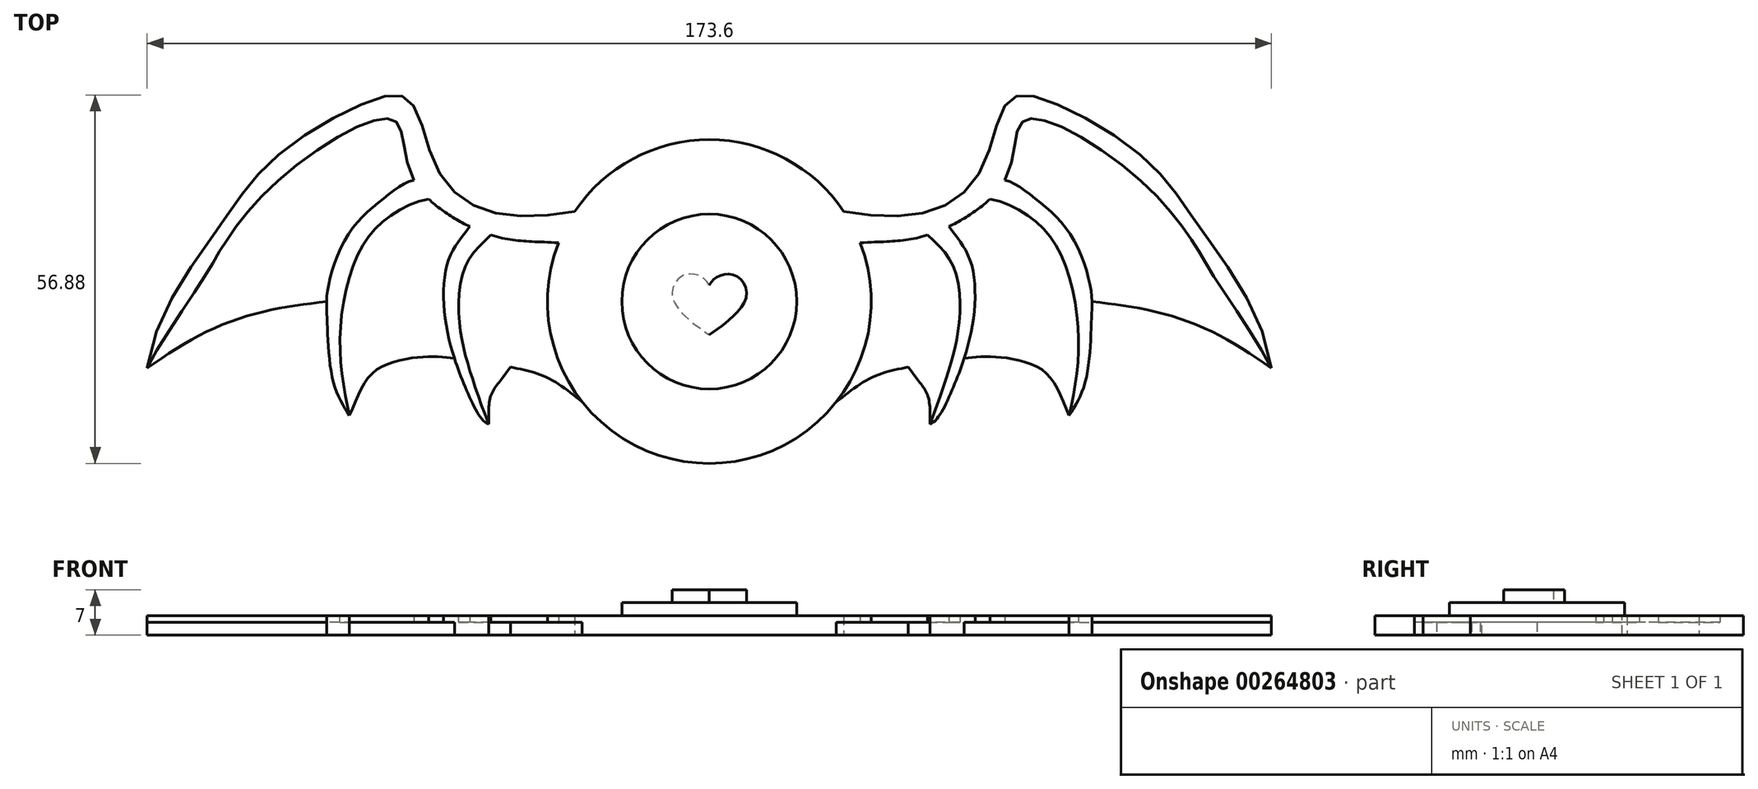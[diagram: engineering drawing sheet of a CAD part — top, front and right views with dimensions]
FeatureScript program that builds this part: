
annotation { "Feature Type Name" : "Feature", "Feature Type Description" : "" }
export const myFeature = defineFeature(function(context is Context, id is Id, definition is map)
    precondition{}
    {
        {
            var Q0;
            Q0=qCreatedBy(makeId("Top.planeOp"),FACE);
            var sketch = newSketch(context, id + "F0", { "sketchPlane" : qUnion([Q0])});
            skCircle(sketch, "E0", {"center": v(0, 0) * mm, "radius": 25 * mm});
            skLineSegment(sketch, "E1", {"start": v(0, 25) * mm, "end": v(0, -25) * mm, "construction": true});
            skFitSpline(sketch, "E2", {"points": [v(20.76, 13.92) * mm, v(34.08, 13.92) * mm, v(42, 20.48) * mm, v(46, 30.69) * mm, v(50.93, 31.48) * mm, v(67.03, 22.24) * mm, v(75.74, 11.46) * mm, v(86.8, -10.28) * mm], "startDerivative": vector(95.75, -17.53) * mm, "endDerivative": vector(18.54, -135.11) * mm});
            skFitSpline(sketch, "E3", {"points": [v(20.7, -14) * mm, v(37, -10.54) * mm, v(45, -8.07) * mm, v(66.66, 1.74) * mm, v(75.74, 11.46) * mm], "startDerivative": vector(59.46, -0.59) * mm, "endDerivative": vector(18.77, 28.66) * mm, "construction": true});
            skFitSpline(sketch, "E4", {"points": [v(23.3, 9.08) * mm, v(33.72, 10.28) * mm, v(45.64, 18.76) * mm, v(47.9, 27.18) * mm, v(51.1, 28.14) * mm, v(65.44, 19.69) * mm, v(74.45, 9.58) * mm, v(78.2, 3.43) * mm, v(86.8, -10.28) * mm], "startDerivative": vector(110.38, 5.87) * mm, "endDerivative": vector(40.39, -81.17) * mm});
            skFitSpline(sketch, "E5", {"points": [v(33.72, 10.28) * mm, v(37.86, 5.02) * mm, v(38.5, -3.9) * mm, v(37, -10.54) * mm, v(34.08, -18.9) * mm], "startDerivative": vector(21.3, -19.5) * mm, "endDerivative": vector(-13.55, -34.2) * mm});
            skFitSpline(sketch, "E6", {"points": [v(37, 11.6) * mm, v(40.25, 6.46) * mm, v(40.52, -4.24) * mm, v(37.2, -14.33) * mm, v(34.08, -18.9) * mm], "startDerivative": vector(14.85, -22) * mm, "endDerivative": vector(-16.96, -5.17) * mm});
            skFitSpline(sketch, "E7", {"points": [v(32.11, -12.01) * mm, v(33.72, -14.49) * mm, v(34.08, -18.9) * mm], "startDerivative": vector(4.43, -5.79) * mm, "endDerivative": vector(-0.15, -8.8) * mm});
            skFitSpline(sketch, "E8", {"points": [v(45.64, 18.76) * mm, v(50.26, 15.97) * mm, v(55.72, 10.44) * mm, v(58.9, 2) * mm, v(59.02, -2.64) * mm, v(58.1, -12.2) * mm, v(55.56, -17.62) * mm], "startDerivative": vector(28.21, -5.42) * mm, "endDerivative": vector(-19.1, -30.2) * mm});
            skFitSpline(sketch, "E9", {"points": [v(43.34, 15.84) * mm, v(49.55, 13.02) * mm, v(53.96, 7.9) * mm, v(56.67, -1.36) * mm, v(56.83, -10.28) * mm, v(55.56, -17.62) * mm], "startDerivative": vector(32.47, -4.35) * mm, "endDerivative": vector(-7.91, -36.84) * mm});
            skFitSpline(sketch, "E10", {"points": [v(38.97, -9.94) * mm, v(46.63, -10.28) * mm, v(52.84, -13.22) * mm, v(55.56, -17.62) * mm], "startDerivative": vector(21.38, 0.7) * mm, "endDerivative": vector(7.12, -15.9) * mm, "construction": true});
            skFitSpline(sketch, "E11", {"points": [v(59.1, 0) * mm, v(68, -1.36) * mm, v(77.72, -4.7) * mm, v(86.8, -10.28) * mm], "startDerivative": vector(27.78, -3.23) * mm, "endDerivative": vector(25.67, -17.5) * mm});
            skFitSpline(sketch, "E12", {"points": [v(19.62, -15.5) * mm, v(25.1, -11.72) * mm, v(30.69, -10.12) * mm], "startDerivative": vector(10.4, 8.3) * mm, "endDerivative": vector(11.78, 2.35) * mm});
            skFitSpline(sketch, "E13", {"points": [v(32.11, -12.01) * mm, v(30.69, -10.12) * mm], "startDerivative": vector(-1.42, 1.9) * mm, "endDerivative": vector(-1.42, 1.9) * mm});
            skFitSpline(sketch, "E14", {"points": [v(55.56, -17.62) * mm, v(52.05, -11.08) * mm, v(46.6, -8.83) * mm, v(42.13, -8.5) * mm, v(39.36, -8.79) * mm], "startDerivative": vector(-10.96, 25.87) * mm, "endDerivative": vector(-14.04, -2.02) * mm});
            skFitSpline(sketch, "E15", {"points": [v(20.76, 13.92) * mm, v(16.18, 9.49) * mm, v(19.62, -15.5) * mm], "startDerivative": vector(-16.85, -9.2) * mm, "endDerivative": vector(11.44, -45.62) * mm});
            skFitSpline(sketch, "E16.MirrorCS", {"points": [v(-20.76, 13.92) * mm, v(-16.18, 9.49) * mm, v(-19.62, -15.5) * mm], "startDerivative": vector(16.85, -9.2) * mm, "endDerivative": vector(-11.44, -45.62) * mm});
            skFitSpline(sketch, "E17.MirrorCS", {"points": [v(-23.3, 9.08) * mm, v(-33.72, 10.28) * mm, v(-45.64, 18.76) * mm, v(-47.9, 27.18) * mm, v(-51.1, 28.14) * mm, v(-65.44, 19.69) * mm, v(-74.45, 9.58) * mm, v(-78.2, 3.43) * mm, v(-86.8, -10.28) * mm], "startDerivative": vector(-110.38, 5.87) * mm, "endDerivative": vector(-40.39, -81.17) * mm});
            skFitSpline(sketch, "E18.MirrorCS", {"points": [v(-20.76, 13.92) * mm, v(-34.08, 13.92) * mm, v(-42, 20.48) * mm, v(-46, 30.69) * mm, v(-50.93, 31.48) * mm, v(-67.03, 22.24) * mm, v(-75.74, 11.46) * mm, v(-86.8, -10.28) * mm], "startDerivative": vector(-95.75, -17.53) * mm, "endDerivative": vector(-18.54, -135.11) * mm});
            skFitSpline(sketch, "E19.MirrorCS", {"points": [v(-33.72, 10.28) * mm, v(-37.86, 5.02) * mm, v(-38.5, -3.9) * mm, v(-37, -10.54) * mm, v(-34.08, -18.9) * mm], "startDerivative": vector(-21.3, -19.5) * mm, "endDerivative": vector(13.55, -34.2) * mm});
            skFitSpline(sketch, "E20.MirrorCS", {"points": [v(-37, 11.6) * mm, v(-40.25, 6.46) * mm, v(-40.52, -4.24) * mm, v(-37.2, -14.33) * mm, v(-34.08, -18.9) * mm], "startDerivative": vector(-14.85, -22) * mm, "endDerivative": vector(16.96, -5.17) * mm});
            skFitSpline(sketch, "E21.MirrorCS", {"points": [v(-43.34, 15.84) * mm, v(-49.55, 13.02) * mm, v(-53.96, 7.9) * mm, v(-56.67, -1.36) * mm, v(-56.83, -10.28) * mm, v(-55.56, -17.62) * mm], "startDerivative": vector(-32.47, -4.35) * mm, "endDerivative": vector(7.91, -36.84) * mm});
            skFitSpline(sketch, "E22.MirrorCS", {"points": [v(-45.64, 18.76) * mm, v(-50.26, 15.97) * mm, v(-55.72, 10.44) * mm, v(-58.9, 2) * mm, v(-59.02, -2.64) * mm, v(-58.1, -12.2) * mm, v(-55.56, -17.62) * mm], "startDerivative": vector(-28.21, -5.42) * mm, "endDerivative": vector(19.1, -30.2) * mm});
            skFitSpline(sketch, "E23.MirrorCS", {"points": [v(-19.62, -15.5) * mm, v(-25.1, -11.72) * mm, v(-30.69, -10.12) * mm], "startDerivative": vector(-10.4, 8.3) * mm, "endDerivative": vector(-11.78, 2.35) * mm});
            skFitSpline(sketch, "E24.MirrorCS", {"points": [v(-32.11, -12.01) * mm, v(-30.69, -10.12) * mm], "startDerivative": vector(1.42, 1.9) * mm, "endDerivative": vector(1.42, 1.9) * mm});
            skFitSpline(sketch, "E25.MirrorCS", {"points": [v(-32.11, -12.01) * mm, v(-33.72, -14.49) * mm, v(-34.08, -18.9) * mm], "startDerivative": vector(-4.43, -5.79) * mm, "endDerivative": vector(0.15, -8.8) * mm});
            skFitSpline(sketch, "E26.MirrorCS", {"points": [v(-59.1, 0) * mm, v(-68, -1.36) * mm, v(-77.72, -4.7) * mm, v(-86.8, -10.28) * mm], "startDerivative": vector(-27.78, -3.23) * mm, "endDerivative": vector(-25.67, -17.5) * mm});
            skFitSpline(sketch, "E27.MirrorCS", {"points": [v(-55.56, -17.62) * mm, v(-52.05, -11.08) * mm, v(-46.6, -8.83) * mm, v(-42.13, -8.5) * mm, v(-39.36, -8.79) * mm], "startDerivative": vector(10.96, 25.87) * mm, "endDerivative": vector(14.04, -2.02) * mm});
            skSolve(sketch);
        }
        {
            var Q0;
            {var subQ0=sQuery(id+"F0.wireOp",EDGE,"E15");Q0=makeQuery(id+"F0.imprint","IMPRINT",FACE,{"disambiguationData":[TD([[makeQuery(id+"F0.imprint","IMPRINT",EDGE,{"derivedFrom":subQ0}),-1.0]])]});}
            var Q1;
            {var subQ0=sQuery(id+"F0.wireOp",EDGE,"E15");Q1=makeQuery(id+"F0.imprint","IMPRINT",FACE,{"disambiguationData":[TD([[makeQuery(id+"F0.imprint","IMPRINT",EDGE,{"derivedFrom":subQ0}),1.0]])]});}
            var Q2;
            {var subQ0=sQuery(id+"F0.wireOp",EDGE,"E16.MirrorCS");Q2=makeQuery(id+"F0.imprint","IMPRINT",FACE,{"disambiguationData":[TD([[makeQuery(id+"F0.imprint","IMPRINT",EDGE,{"derivedFrom":subQ0}),-1.0]])]});}
            extrude(context, id + "F1", {"entities" : qUnion([Q0, Q1, Q2]), "depth" : 3 * mm, "offsetDistance" : 25 * mm});
        }
        {
            var Q0;
            Q0=qCreatedBy(makeId("Top.planeOp"),FACE);
            var sketch = newSketch(context, id + "F2", { "sketchPlane" : qUnion([Q0])});
            skCircle(sketch, "E28", {"center": v(0, 0) * mm, "radius": 13.5 * mm});
            skSolve(sketch);
        }
        {
            var Q0;
            Q0=qSketchRegion(id+"F2",true);
            extrude(context, id + "F3", {"entities" : qUnion([Q0]), "operationType" : NewBodyOperationType.ADD, "depth" : 5 * mm, "offsetDistance" : 25 * mm});
        }
        {
            var Q0;
            {var subQ4=sQuery(id+"F0.wireOp",EDGE,"E2");Q0=makeQuery(id+"F0.imprint","IMPRINT",FACE,{"disambiguationData":[TD([[makeQuery(id+"F0.imprint","IMPRINT",EDGE,{"derivedFrom":subQ4}),-1.0]])]});}
            var Q1;
            {var subQ0=sQuery(id+"F0.wireOp",EDGE,"E15");Q1=makeQuery(id+"F0.imprint","IMPRINT",FACE,{"disambiguationData":[TD([[makeQuery(id+"F0.imprint","IMPRINT",EDGE,{"derivedFrom":subQ0}),1.0]])]});}
            var Q2;
            {var subQ0=sQuery(id+"F0.wireOp",EDGE,"E5");Q2=makeQuery(id+"F0.imprint","IMPRINT",FACE,{"disambiguationData":[TD([[makeQuery(id+"F0.imprint","IMPRINT",EDGE,{"derivedFrom":subQ0}),-1.0]])]});}
            var Q3;
            {var subQ0=sQuery(id+"F0.wireOp",EDGE,"E5");Q3=makeQuery(id+"F0.imprint","IMPRINT",FACE,{"disambiguationData":[TD([[makeQuery(id+"F0.imprint","IMPRINT",EDGE,{"derivedFrom":subQ0}),1.0]])]});}
            var Q4;
            {var subQ3=sQuery(id+"F0.wireOp",EDGE,"E9");Q4=makeQuery(id+"F0.imprint","IMPRINT",FACE,{"disambiguationData":[TD([[makeQuery(id+"F0.imprint","IMPRINT",EDGE,{"derivedFrom":subQ3}),-1.0]])]});}
            var Q5;
            {var subQ3=sQuery(id+"F0.wireOp",EDGE,"E9");Q5=makeQuery(id+"F0.imprint","IMPRINT",FACE,{"disambiguationData":[TD([[makeQuery(id+"F0.imprint","IMPRINT",EDGE,{"derivedFrom":subQ3}),1.0]])]});}
            var Q6;
            {var subQ0=sQuery(id+"F0.wireOp",EDGE,"E11");Q6=makeQuery(id+"F0.imprint","IMPRINT",FACE,{"disambiguationData":[TD([[makeQuery(id+"F0.imprint","IMPRINT",EDGE,{"derivedFrom":subQ0}),1.0]])]});}
            var Q7;
            {var subQ1=sQuery(id+"F0.wireOp",EDGE,"E19.MirrorCS");Q7=makeQuery(id+"F0.imprint","IMPRINT",FACE,{"disambiguationData":[TD([[makeQuery(id+"F0.imprint","IMPRINT",EDGE,{"derivedFrom":subQ1}),1.0]])]});}
            var Q8;
            {var subQ3=sQuery(id+"F0.wireOp",EDGE,"E21.MirrorCS");Q8=makeQuery(id+"F0.imprint","IMPRINT",FACE,{"disambiguationData":[TD([[makeQuery(id+"F0.imprint","IMPRINT",EDGE,{"derivedFrom":subQ3}),1.0]])]});}
            var Q9;
            {var subQ0=sQuery(id+"F0.wireOp",EDGE,"E19.MirrorCS");Q9=makeQuery(id+"F0.imprint","IMPRINT",FACE,{"disambiguationData":[TD([[makeQuery(id+"F0.imprint","IMPRINT",EDGE,{"derivedFrom":subQ0}),-1.0]])]});}
            var Q10;
            {var subQ6=sQuery(id+"F0.wireOp",EDGE,"E18.MirrorCS");Q10=makeQuery(id+"F0.imprint","IMPRINT",FACE,{"disambiguationData":[TD([[makeQuery(id+"F0.imprint","IMPRINT",EDGE,{"derivedFrom":subQ6}),1.0]])]});}
            var Q11;
            {var subQ0=sQuery(id+"F0.wireOp",EDGE,"E26.MirrorCS");Q11=makeQuery(id+"F0.imprint","IMPRINT",FACE,{"disambiguationData":[TD([[makeQuery(id+"F0.imprint","IMPRINT",EDGE,{"derivedFrom":subQ0}),-1.0]])]});}
            var Q12;
            {var subQ0=sQuery(id+"F0.wireOp",EDGE,"E21.MirrorCS");Q12=makeQuery(id+"F0.imprint","IMPRINT",FACE,{"disambiguationData":[TD([[makeQuery(id+"F0.imprint","IMPRINT",EDGE,{"derivedFrom":subQ0}),-1.0]])]});}
            var Q13;
            {var subQ0=sQuery(id+"F0.wireOp",EDGE,"E16.MirrorCS");Q13=makeQuery(id+"F0.imprint","IMPRINT",FACE,{"disambiguationData":[TD([[makeQuery(id+"F0.imprint","IMPRINT",EDGE,{"derivedFrom":subQ0}),-1.0]])]});}
            extrude(context, id + "F4", {"entities" : qUnion([Q0, Q1, Q2, Q3, Q4, Q5, Q6, Q7, Q8, Q9, Q10, Q11, Q12, Q13]), "operationType" : NewBodyOperationType.ADD, "depth" : 2 * mm, "offsetDistance" : 25 * mm});
        }
        {
            var Q0;
            {var subQ4=sQuery(id+"F0.wireOp",EDGE,"E2");Q0=makeQuery(id+"F0.imprint","IMPRINT",FACE,{"disambiguationData":[TD([[makeQuery(id+"F0.imprint","IMPRINT",EDGE,{"derivedFrom":subQ4}),-1.0]])]});}
            var Q1;
            {var subQ0=sQuery(id+"F0.wireOp",EDGE,"E5");Q1=makeQuery(id+"F0.imprint","IMPRINT",FACE,{"disambiguationData":[TD([[makeQuery(id+"F0.imprint","IMPRINT",EDGE,{"derivedFrom":subQ0}),1.0]])]});}
            var Q2;
            {var subQ3=sQuery(id+"F0.wireOp",EDGE,"E9");Q2=makeQuery(id+"F0.imprint","IMPRINT",FACE,{"disambiguationData":[TD([[makeQuery(id+"F0.imprint","IMPRINT",EDGE,{"derivedFrom":subQ3}),1.0]])]});}
            var Q3;
            {var subQ6=sQuery(id+"F0.wireOp",EDGE,"E18.MirrorCS");Q3=makeQuery(id+"F0.imprint","IMPRINT",FACE,{"disambiguationData":[TD([[makeQuery(id+"F0.imprint","IMPRINT",EDGE,{"derivedFrom":subQ6}),1.0]])]});}
            var Q4;
            {var subQ0=sQuery(id+"F0.wireOp",EDGE,"E19.MirrorCS");Q4=makeQuery(id+"F0.imprint","IMPRINT",FACE,{"disambiguationData":[TD([[makeQuery(id+"F0.imprint","IMPRINT",EDGE,{"derivedFrom":subQ0}),-1.0]])]});}
            var Q5;
            {var subQ0=sQuery(id+"F0.wireOp",EDGE,"E21.MirrorCS");Q5=makeQuery(id+"F0.imprint","IMPRINT",FACE,{"disambiguationData":[TD([[makeQuery(id+"F0.imprint","IMPRINT",EDGE,{"derivedFrom":subQ0}),-1.0]])]});}
            extrude(context, id + "F5", {"entities" : qUnion([Q0, Q1, Q2, Q3, Q4, Q5]), "operationType" : NewBodyOperationType.ADD, "depth" : 3 * mm, "offsetDistance" : 25 * mm});
        }
        {
            var Q0;
            Q0=makeQuery(id+"F3.opExtrude","CAP_FACE",FACE,{"disambiguationData":[OSD([sQuery(id+"F2.wireOp",EDGE,"E28")])],"isStart":false});
            var sketch = newSketch(context, id + "F6", { "sketchPlane" : qUnion([Q0])});
            skFitSpline(sketch, "E29", {"points": [v(0, 2.56) * mm, v(-1.46, 3.94) * mm, v(-4.21, 3.94) * mm, v(-5.75, 0.99) * mm, v(-3.12, -2.8) * mm, v(0, -5.13) * mm], "startDerivative": vector(-7.08, 12.17) * mm, "endDerivative": vector(14.96, -10.49) * mm});
            skFitSpline(sketch, "E30.MirrorCS", {"points": [v(0, 2.56) * mm, v(1.46, 3.94) * mm, v(4.21, 3.94) * mm, v(5.75, 0.99) * mm, v(3.12, -2.8) * mm, v(0, -5.13) * mm], "startDerivative": vector(7.08, 12.17) * mm, "endDerivative": vector(-14.96, -10.49) * mm});
            skSolve(sketch);
        }
        {
            var Q0;
            Q0=makeQuery(id+"F6.imprint","IMPRINT",FACE,{"disambiguationData":[TD([[makeQuery(id+"F6.imprint","IMPRINT",EDGE,{"derivedFrom":sQuery(id+"F6.wireOp",EDGE,"E29")}),1.0]])]});
            extrude(context, id + "F7", {"entities" : qUnion([Q0]), "operationType" : NewBodyOperationType.ADD, "depth" : 2 * mm, "offsetDistance" : 25 * mm});
        }
    });
